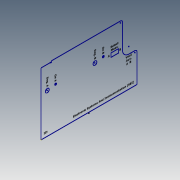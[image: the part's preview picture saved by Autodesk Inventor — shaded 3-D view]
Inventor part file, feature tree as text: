
AUTODESK INVENTOR PART (.ipt)
format: ipt  version: 2020.5 (Build 245400000, 400)  size: 159,232 bytes
history: native  units: mm
features: sketch x1
ambient origin geometry x8: Origin, YZ Plane, XZ Plane, XY Plane, X Axis, Y Axis, Z Axis, Center Point
feature tree (1):
  sketch  "Sketch33"  dims[d13=18.0mm d14=60.0mm d804=2.6mm d805=9.1mm d806=2.099988mm d807=6.7mm d808=45.55mm d809=45.050107mm d810=36.050101mm d811=46.020973mm d812=2.6mm d813=9.1mm d814=2.099988mm d815=6.7mm d816=45.55mm d817=4.949893mm d818=13.949899mm d819=46.020973mm d820=8.5mm d821=2.1mm d822=2.1mm d823=7.9mm d824=44.306mm d825=23.049893mm d826=22.749893mm d827=47.406mm d828=2.1mm d829=2.0mm d830=2.0mm d831=2.1mm d832=19.999893mm d833=40.256mm d834=40.256mm d835=31.999893mm d836=6.0mm d837=6.5mm d838=2.1mm d839=2.1mm d840=26.7mm d841=38.919893mm d842=38.669893mm d843=29.8mm d844=4.3mm d845=2.1mm d846=6.0mm d847=47.292893mm d848=2.7mm d849=63.873077mm d850=6.0mm d851=47.292893mm d852=2.1mm d853=5.4mm d854=39.219893mm d855=23.6mm]
